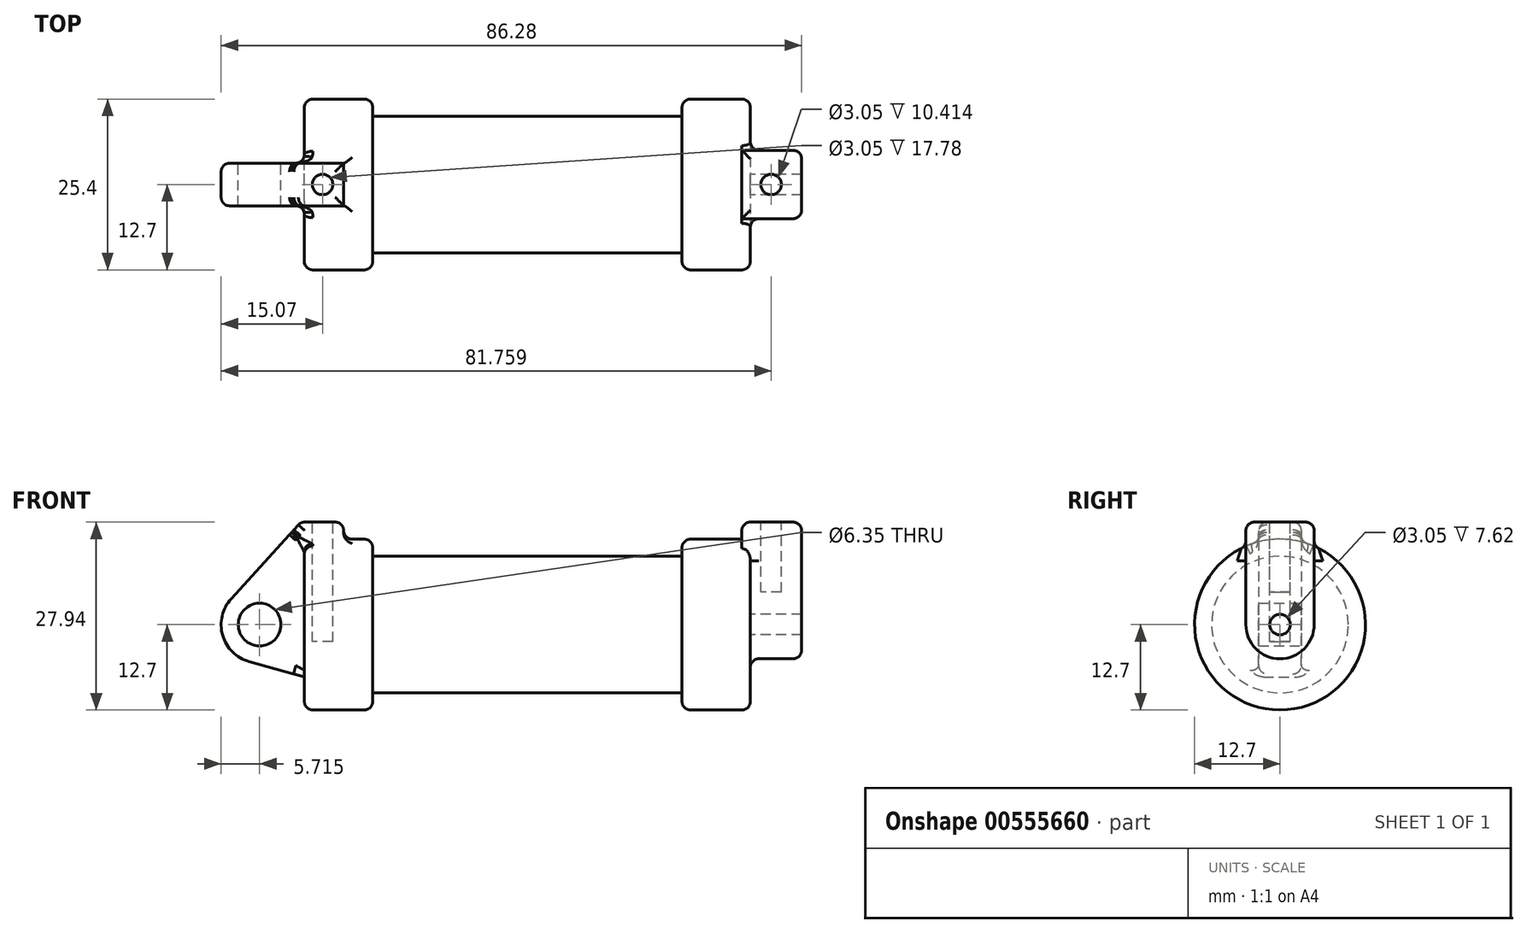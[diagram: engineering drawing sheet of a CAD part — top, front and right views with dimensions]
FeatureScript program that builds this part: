
annotation { "Feature Type Name" : "Feature", "Feature Type Description" : "" }
export const myFeature = defineFeature(function(context is Context, id is Id, definition is map)
    precondition{}
    {
        {
            var Q0;
            Q0=qCreatedBy(makeId("Front.planeOp"),FACE);
            var sketch = newSketch(context, id + "F0", { "sketchPlane" : qUnion([Q0])});
            skLineSegment(sketch, "E0", {"start": v(0, 0) * mm, "end": v(0, 12.7) * mm});
            skLineSegment(sketch, "E1", {"start": v(0, 12.7) * mm, "end": v(10.16, 12.7) * mm});
            skLineSegment(sketch, "E2", {"start": v(10.16, 12.7) * mm, "end": v(10.16, 10.16) * mm});
            skLineSegment(sketch, "E3", {"start": v(10.16, 10.16) * mm, "end": v(56.13, 10.16) * mm});
            skLineSegment(sketch, "E4", {"start": v(56.13, 10.16) * mm, "end": v(56.13, 12.7) * mm});
            skLineSegment(sketch, "E5", {"start": v(56.13, 12.7) * mm, "end": v(66.3, 12.7) * mm});
            skLineSegment(sketch, "E6", {"start": v(66.3, 12.7) * mm, "end": v(66.3, 0) * mm});
            skLineSegment(sketch, "E7", {"start": v(66.3, 0) * mm, "end": v(0, 0) * mm});
            skLineSegment(sketch, "E8", {"start": v(5.84, 15.24) * mm, "end": v(-0.5, 15.24) * mm});
            skLineSegment(sketch, "E9", {"start": v(-0.5, 15.24) * mm, "end": v(-10.88, 3.85) * mm});
            skLineSegment(sketch, "E10", {"start": v(0, 0) * mm, "end": v(-6.65, 0) * mm});
            skCircle(sketch, "E11", {"center": v(-6.65, 0) * mm, "radius": 5.72 * mm});
            skCircle(sketch, "E12", {"center": v(-6.65, 0) * mm, "radius": 3.18 * mm});
            skLineSegment(sketch, "E13", {"start": v(5.84, 15.24) * mm, "end": v(5.84, -9.4) * mm});
            skLineSegment(sketch, "E14", {"start": v(5.84, -9.4) * mm, "end": v(-8.18, -5.5) * mm});
            skSolve(sketch);
        }
        {
            var Q0;
            {var subQ0=sQuery(id+"F0.wireOp",EDGE,"E2");Q0=makeQuery(id+"F0.imprint","IMPRINT",FACE,{"disambiguationData":[TD([[makeQuery(id+"F0.imprint","IMPRINT",EDGE,{"derivedFrom":subQ0}),-1.0]])]});}
            var Q1;
            Q1=sQuery(id+"F0.wireOp",EDGE,"E7");
            revolve(context, id + "F1", {"entities" : qUnion([Q0]), "axis" : qUnion([Q1]), "revolveType" : RevolveType.FULL});
        }
        {
            var Q0;
            {var subQ0=sQuery(id+"F0.wireOp",EDGE,"E0");Q0=makeQuery(id+"F0.imprint","IMPRINT",FACE,{"disambiguationData":[TD([[makeQuery(id+"F0.imprint","IMPRINT",EDGE,{"derivedFrom":subQ0}),-1.0]])]});}
            var Q1;
            Q1=sQuery(id+"F0.wireOp",EDGE,"E7");
            revolve(context, id + "F2", {"operationType" : NewBodyOperationType.ADD, "entities" : qUnion([Q0]), "axis" : qUnion([Q1]), "revolveType" : RevolveType.FULL});
        }
        {
            var Q0;
            {var subQ0=sQuery(id+"F0.wireOp",EDGE,"E14");Q0=makeQuery(id+"F0.imprint","IMPRINT",FACE,{"disambiguationData":[TD([[makeQuery(id+"F0.imprint","IMPRINT",EDGE,{"derivedFrom":subQ0}),-1.0]])]});}
            var Q1;
            {var subQ5=sQuery(id+"F0.wireOp",EDGE,"E12");Q1=makeQuery(id+"F0.imprint","IMPRINT",FACE,{"disambiguationData":[TD([[makeQuery(id+"F0.imprint","IMPRINT",EDGE,{"derivedFrom":subQ5}),-1.0]])]});}
            extrude(context, id + "F3", {"entities" : qUnion([Q0, Q1]), "operationType" : NewBodyOperationType.ADD, "endBound" : BoundingType.SYMMETRIC, "depth" : 6.35 * mm, "offsetDistance" : 25.4 * mm});
        }
        {
            var Q0;
            Q0=makeQuery(id+"F1.opRevolve","SWEPT_FACE",FACE,{"disambiguationData":[OSD([sQuery(id+"F0.wireOp",EDGE,"E6")])]});
            var sketch = newSketch(context, id + "F4", { "sketchPlane" : qUnion([Q0])});
            skCircle(sketch, "E15", {"center": v(0, 0) * mm, "radius": 5.08 * mm});
            skCircle(sketch, "E16", {"center": v(0, 0) * mm, "radius": 1.52 * mm});
            skLineSegment(sketch, "E17", {"start": v(-5.08, 0) * mm, "end": v(-5.08, 15.24) * mm});
            skLineSegment(sketch, "E18", {"start": v(-5.08, 15.24) * mm, "end": v(5.08, 15.24) * mm});
            skLineSegment(sketch, "E19", {"start": v(5.08, 15.24) * mm, "end": v(5.08, 0) * mm});
            skSolve(sketch);
        }
        {
            var Q0;
            {var subQ0=sQuery(id+"F4.wireOp",EDGE,"E17");var subQ1=sQuery(id+"F4.wireOp",EDGE,"E15");var subQ2=makeQuery(id+"F4.imprint","INTERSECT",VERTEX,{"derivedFrom":[subQ1,subQ0]});Q0=makeQuery(id+"F4.imprint","IMPRINT",FACE,{"disambiguationData":[TD([[makeQuery(id+"F4.imprint","IMPRINT",EDGE,{"disambiguationData":[TD([[subQ2,1.0]])],"derivedFrom":subQ1}),-1.0]])]});}
            var Q1;
            {var subQ0=sQuery(id+"F4.wireOp",EDGE,"E18");Q1=makeQuery(id+"F4.imprint","IMPRINT",FACE,{"disambiguationData":[TD([[makeQuery(id+"F4.imprint","IMPRINT",EDGE,{"derivedFrom":subQ0}),-1.0]])]});}
            var Q2;
            Q2=makeQuery(id+"F4.imprint","IMPRINT",FACE,{"disambiguationData":[TD([[makeQuery(id+"F4.imprint","IMPRINT",EDGE,{"derivedFrom":sQuery(id+"F4.wireOp",EDGE,"E16")}),-1.0]])]});
            extrude(context, id + "F5", {"entities" : qUnion([Q0, Q1, Q2]), "operationType" : NewBodyOperationType.ADD, "depth" : 7.62 * mm, "offsetDistance" : 25.4 * mm});
        }
        {
            var Q0;
            Q0=makeQuery(id+"F5.opExtrude","CAP_FACE",FACE,{"disambiguationData":[OSD([sQuery(id+"F4.wireOp",EDGE,"E15"),sQuery(id+"F4.wireOp",EDGE,"E16"),sQuery(id+"F4.wireOp",EDGE,"E17"),sQuery(id+"F4.wireOp",EDGE,"E18"),sQuery(id+"F4.wireOp",EDGE,"E19")])],"isStart":true});
            extrude(context, id + "F6", {"entities" : qUnion([Q0]), "operationType" : NewBodyOperationType.ADD, "depth" : 1.27 * mm, "offsetDistance" : 25.4 * mm});
        }
        {
            var Q0;
            {var subQ0=sQuery(id+"F4.wireOp",EDGE,"E18");Q0=makeQuery(id+"F6.boolean.opBoolean","MERGE",FACE,{"derivedFrom":[makeQuery(id+"F5.opExtrude","SWEPT_FACE",FACE,{"disambiguationData":[OSD([subQ0])]}),makeQuery(id+"F6.opExtrude","SWEPT_FACE",FACE,{"disambiguationData":[OSD([subQ0])]})]});}
            var sketch = newSketch(context, id + "F7", { "sketchPlane" : qUnion([Q0])});
            skCircle(sketch, "E20", {"center": v(69.39, 0) * mm, "radius": 1.52 * mm});
            skSolve(sketch);
        }
        {
            var Q0;
            Q0=makeQuery(id+"F7.imprint","IMPRINT",FACE,{"disambiguationData":[TD([[makeQuery(id+"F7.imprint","IMPRINT",EDGE,{"derivedFrom":sQuery(id+"F7.wireOp",EDGE,"E20")}),1.0]])]});
            extrude(context, id + "F8", {"entities" : qUnion([Q0]), "operationType" : NewBodyOperationType.REMOVE, "oppositeDirection" : true, "depth" : 10.4 * mm, "offsetDistance" : 25.4 * mm});
        }
        {
            var Q0;
            {var subQ1=sQuery(id+"F0.wireOp",EDGE,"E0");Q0=makeQuery(id+"F0.imprint","IMPRINT",FACE,{"disambiguationData":[TD([[makeQuery(id+"F0.imprint","IMPRINT",EDGE,{"derivedFrom":subQ1}),1.0]])]});}
            var Q1;
            {var subQ5=sQuery(id+"F0.wireOp",EDGE,"E12");Q1=makeQuery(id+"F0.imprint","IMPRINT",FACE,{"disambiguationData":[TD([[makeQuery(id+"F0.imprint","IMPRINT",EDGE,{"derivedFrom":subQ5}),-1.0]])]});}
            extrude(context, id + "F9", {"entities" : qUnion([Q0, Q1]), "endBound" : BoundingType.SYMMETRIC, "depth" : 6.35 * mm, "offsetDistance" : 25.4 * mm});
        }
        {
            var Q0;
            Q0=makeQuery(id+"F9.opExtrude","SWEPT_FACE",FACE,{"disambiguationData":[OSD([sQuery(id+"F0.wireOp",EDGE,"E1")])]});
            extrude(context, id + "F10", {"entities" : qUnion([Q0]), "operationType" : NewBodyOperationType.ADD, "depth" : 4.57 * mm, "offsetDistance" : 25.4 * mm});
        }
        {
            var Q0;
            Q0=makeQuery(id+"F9.opExtrude","SWEPT_FACE",FACE,{"disambiguationData":[OSD([sQuery(id+"F0.wireOp",EDGE,"E8")])]});
            var sketch = newSketch(context, id + "F11", { "sketchPlane" : qUnion([Q0])});
            skCircle(sketch, "E21", {"center": v(2.7, 0) * mm, "radius": 1.52 * mm});
            skSolve(sketch);
        }
        {
            var Q0;
            Q0=makeQuery(id+"F11.imprint","IMPRINT",FACE,{"disambiguationData":[TD([[makeQuery(id+"F11.imprint","IMPRINT",EDGE,{"derivedFrom":sQuery(id+"F11.wireOp",EDGE,"E21")}),1.0]])]});
            extrude(context, id + "F12", {"entities" : qUnion([Q0]), "operationType" : NewBodyOperationType.REMOVE, "oppositeDirection" : true, "depth" : 17.78 * mm, "offsetDistance" : 25.4 * mm});
        }
        {
            var Q0;
            {var subQ0=sQuery(id+"F0.wireOp",EDGE,"E1");Q0=makeQuery(id+"F10.boolean.opBoolean","INTERSECT",EDGE,{"derivedFrom":[makeQuery(id+"F2.opRevolve","SWEPT_FACE",FACE,{"disambiguationData":[OSD([sQuery(id+"F0.wireOp",EDGE,"E0")])]}),makeQuery(id+"F10.opExtrude","SWEPT_FACE",FACE,{"disambiguationData":[OSD([subQ0]),TDD([makeQuery(id+"F9.opExtrude","CAP_EDGE",EDGE,{"disambiguationData":[OSD([subQ0])],"isStart":false})])]})]});}
            var Q1;
            {var subQ0=sQuery(id+"F0.wireOp",EDGE,"E1");Q1=makeQuery(id+"F10.boolean.opBoolean","INTERSECT",EDGE,{"derivedFrom":[makeQuery(id+"F2.boolean.opBoolean","MERGE",FACE,{"derivedFrom":[makeQuery(id+"F1.opRevolve","SWEPT_FACE",FACE,{"disambiguationData":[OSD([subQ0])]}),makeQuery(id+"F2.opRevolve","SWEPT_FACE",FACE,{"disambiguationData":[OSD([subQ0])]})]}),makeQuery(id+"F10.opExtrude","SWEPT_FACE",FACE,{"disambiguationData":[OSD([subQ0]),TDD([makeQuery(id+"F9.opExtrude","CAP_EDGE",EDGE,{"disambiguationData":[OSD([subQ0])],"isStart":false})])]})]});}
            var Q2;
            {var subQ0=sQuery(id+"F0.wireOp",EDGE,"E1");Q2=makeQuery(id+"F10.boolean.opBoolean","INTERSECT",EDGE,{"derivedFrom":[makeQuery(id+"F2.boolean.opBoolean","MERGE",FACE,{"derivedFrom":[makeQuery(id+"F1.opRevolve","SWEPT_FACE",FACE,{"disambiguationData":[OSD([subQ0])]}),makeQuery(id+"F2.opRevolve","SWEPT_FACE",FACE,{"disambiguationData":[OSD([subQ0])]})]}),makeQuery(id+"F10.opExtrude","SWEPT_FACE",FACE,{"disambiguationData":[OSD([subQ0,sQuery(id+"F0.wireOp",EDGE,"E13")])]})]});}
            var Q3;
            {var subQ0=sQuery(id+"F0.wireOp",EDGE,"E1");Q3=makeQuery(id+"F10.boolean.opBoolean","INTERSECT",EDGE,{"derivedFrom":[makeQuery(id+"F2.boolean.opBoolean","MERGE",FACE,{"derivedFrom":[makeQuery(id+"F1.opRevolve","SWEPT_FACE",FACE,{"disambiguationData":[OSD([subQ0])]}),makeQuery(id+"F2.opRevolve","SWEPT_FACE",FACE,{"disambiguationData":[OSD([subQ0])]})]}),makeQuery(id+"F10.opExtrude","SWEPT_FACE",FACE,{"disambiguationData":[OSD([subQ0]),TDD([makeQuery(id+"F9.opExtrude","CAP_EDGE",EDGE,{"disambiguationData":[OSD([subQ0])],"isStart":true})])]})]});}
            var Q4;
            {var subQ0=sQuery(id+"F0.wireOp",EDGE,"E1");Q4=makeQuery(id+"F10.boolean.opBoolean","INTERSECT",EDGE,{"derivedFrom":[makeQuery(id+"F2.opRevolve","SWEPT_FACE",FACE,{"disambiguationData":[OSD([sQuery(id+"F0.wireOp",EDGE,"E0")])]}),makeQuery(id+"F10.opExtrude","SWEPT_FACE",FACE,{"disambiguationData":[OSD([subQ0]),TDD([makeQuery(id+"F9.opExtrude","CAP_EDGE",EDGE,{"disambiguationData":[OSD([subQ0])],"isStart":true})])]})]});}
            fillet(context, id + "F13", {"entities" : qUnion([Q0, Q1, Q2, Q3, Q4]), "radius" : 1.27 * mm, "tangentPropagation" : true, "allowEdgeOverflow" : false});
        }
        {
            var Q0;
            Q0=makeQuery(id+"F3.opExtrude","CAP_EDGE",EDGE,{"disambiguationData":[OSD([sQuery(id+"F0.wireOp",EDGE,"E14")])],"isStart":false});
            fillet(context, id + "F14", {"entities" : qUnion([Q0]), "radius" : 1.27 * mm, "tangentPropagation" : true, "allowEdgeOverflow" : false});
        }
        {
            var Q0;
            Q0=makeQuery(id+"F9.opExtrude","CAP_EDGE",EDGE,{"disambiguationData":[OSD([sQuery(id+"F0.wireOp",EDGE,"E8")])],"isStart":false});
            var Q1;
            Q1=makeQuery(id+"F9.opExtrude","SWEPT_EDGE",EDGE,{"disambiguationData":[OSD([sQuery(id+"F0.wireOp",EDGE,"E8"),sQuery(id+"F0.wireOp",EDGE,"E13")])]});
            var Q2;
            Q2=makeQuery(id+"F9.opExtrude","CAP_EDGE",EDGE,{"disambiguationData":[OSD([sQuery(id+"F0.wireOp",EDGE,"E8")])],"isStart":true});
            var Q3;
            Q3=makeQuery(id+"F9.opExtrude","CAP_EDGE",EDGE,{"disambiguationData":[OSD([sQuery(id+"F0.wireOp",EDGE,"E9")])],"isStart":true});
            fillet(context, id + "F15", {"entities" : qUnion([Q0, Q1, Q2, Q3]), "radius" : 1.27 * mm, "tangentPropagation" : true, "allowEdgeOverflow" : false});
        }
        {
            var Q0;
            Q0=makeQuery(id+"F1.opRevolve","SWEPT_EDGE",EDGE,{"disambiguationData":[OSD([sQuery(id+"F0.wireOp",EDGE,"E1"),sQuery(id+"F0.wireOp",EDGE,"E2")])]});
            var Q1;
            Q1=makeQuery(id+"F2.opRevolve","SWEPT_EDGE",EDGE,{"disambiguationData":[OSD([sQuery(id+"F0.wireOp",EDGE,"E0"),sQuery(id+"F0.wireOp",EDGE,"E1")])]});
            fillet(context, id + "F16", {"entities" : qUnion([Q0, Q1]), "radius" : 1.27 * mm, "tangentPropagation" : true, "allowEdgeOverflow" : false});
        }
        {
            var Q0;
            Q0=makeQuery(id+"F1.opRevolve","SWEPT_EDGE",EDGE,{"disambiguationData":[OSD([sQuery(id+"F0.wireOp",EDGE,"E4"),sQuery(id+"F0.wireOp",EDGE,"E5")])]});
            var Q1;
            {var subQ0=sQuery(id+"F0.wireOp",EDGE,"E5");var subQ1=sQuery(id+"F0.wireOp",EDGE,"E6");Q1=makeQuery(id+"F5.boolean.opBoolean","SPLIT",EDGE,{"disambiguationData":[topologyDisambiguationEdgeConnected([makeQuery(id+"F1.opRevolve","SWEPT_FACE",FACE,{"disambiguationData":[OSD([subQ1])]})])],"derivedFrom":makeQuery(id+"F1.opRevolve","SWEPT_EDGE",EDGE,{"disambiguationData":[OSD([subQ0,subQ1])]})});}
            fillet(context, id + "F17", {"entities" : qUnion([Q0, Q1]), "radius" : 1.27 * mm, "tangentPropagation" : true, "allowEdgeOverflow" : false});
        }
        {
            var Q0;
            Q0=makeQuery(id+"F6.opExtrude","CAP_EDGE",EDGE,{"disambiguationData":[OSD([sQuery(id+"F0.wireOp",EDGE,"E5"),sQuery(id+"F0.wireOp",EDGE,"E6")])],"isStart":false});
            var Q1;
            {var subQ0=sQuery(id+"F4.wireOp",EDGE,"E19");var subQ1=sQuery(id+"F0.wireOp",EDGE,"E5");var subQ2=sQuery(id+"F0.wireOp",EDGE,"E6");Q1=makeQuery(id+"F17.opFillet","BLEND_EDGE",EDGE,{"blendedFrom":[makeQuery(id+"F5.boolean.opBoolean","SPLIT",EDGE,{"disambiguationData":[topologyDisambiguationEdgeConnected([makeQuery(id+"F1.opRevolve","SWEPT_FACE",FACE,{"disambiguationData":[OSD([subQ2])]})])],"derivedFrom":makeQuery(id+"F1.opRevolve","SWEPT_EDGE",EDGE,{"disambiguationData":[OSD([subQ1,subQ2])]})}),makeQuery(id+"F6.boolean.opBoolean","MERGE",FACE,{"derivedFrom":[makeQuery(id+"F5.opExtrude","SWEPT_FACE",FACE,{"disambiguationData":[OSD([subQ0])]}),makeQuery(id+"F6.opExtrude","SWEPT_FACE",FACE,{"disambiguationData":[OSD([subQ0])]})]})],"blendedInto":[makeQuery(id+"F6.boolean.opBoolean","MERGE",FACE,{"derivedFrom":[makeQuery(id+"F5.opExtrude","SWEPT_FACE",FACE,{"disambiguationData":[OSD([subQ0])]}),makeQuery(id+"F6.opExtrude","SWEPT_FACE",FACE,{"disambiguationData":[OSD([subQ0])]})]})]});}
            var Q2;
            Q2=makeQuery(id+"F5.opExtrude","CAP_EDGE",EDGE,{"disambiguationData":[OSD([sQuery(id+"F4.wireOp",EDGE,"E19")])],"isStart":false});
            var Q3;
            {var subQ0=sQuery(id+"F4.wireOp",EDGE,"E18");var subQ1=sQuery(id+"F4.wireOp",EDGE,"E17");Q3=makeQuery(id+"F6.boolean.opBoolean","MERGE",EDGE,{"derivedFrom":[makeQuery(id+"F5.opExtrude","SWEPT_EDGE",EDGE,{"disambiguationData":[OSD([subQ1,subQ0])]}),makeQuery(id+"F6.opExtrude","SWEPT_EDGE",EDGE,{"disambiguationData":[OSD([subQ1,subQ0])]})]});}
            var Q4;
            Q4=makeQuery(id+"F5.opExtrude","CAP_EDGE",EDGE,{"disambiguationData":[OSD([sQuery(id+"F4.wireOp",EDGE,"E18")])],"isStart":false});
            var Q5;
            {var subQ0=sQuery(id+"F4.wireOp",EDGE,"E19");var subQ1=sQuery(id+"F4.wireOp",EDGE,"E18");Q5=makeQuery(id+"F6.boolean.opBoolean","MERGE",EDGE,{"derivedFrom":[makeQuery(id+"F5.opExtrude","SWEPT_EDGE",EDGE,{"disambiguationData":[OSD([subQ1,subQ0])]}),makeQuery(id+"F6.opExtrude","SWEPT_EDGE",EDGE,{"disambiguationData":[OSD([subQ1,subQ0])]})]});}
            var Q6;
            Q6=makeQuery(id+"F6.opExtrude","CAP_EDGE",EDGE,{"disambiguationData":[OSD([sQuery(id+"F4.wireOp",EDGE,"E18")])],"isStart":false});
            fillet(context, id + "F18", {"entities" : qUnion([Q0, Q1, Q2, Q3, Q4, Q5, Q6]), "radius" : 1.27 * mm, "tangentPropagation" : true, "allowEdgeOverflow" : false});
        }
    });
